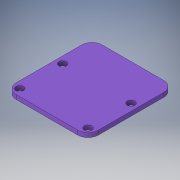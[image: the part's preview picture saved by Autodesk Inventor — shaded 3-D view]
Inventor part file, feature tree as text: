
AUTODESK INVENTOR PART (.ipt)
format: ipt  version: 2019.2 (Build 232265000, 265)  size: 130,048 bytes
history: native  units: in
note: dims shown in document units (in); Inventor stores cm internally (conversion verified against a paired STEP export)
features: sketch x2, extrude x1, fillet x1, hole x1
ambient origin geometry x8: Origin, YZ Plane, XZ Plane, XY Plane, X Axis, Y Axis, Z Axis, Center Point
bodies: Solid1 (feature_tree)
feature tree (5):
  extrude  "Extrusion1"  Depth=0.9843in
  fillet  "Fillet1"  Radius=0.05in
  hole  "Hole2"  [1 undecoded]
  sketch  "Sketch1"  dims[d0=0.9394in d1=0.9843in d4=0.05in d5=0.0in]
  sketch  "Sketch3"  dims[d15=0.1181in d16=0.0787in d17=0.0787in d18=0.0787in d19=0.5709in d20=0.0866in d21=0.75in d22=0.375in d23=0.25in d24=0.5635in d25=1.0in d26=0.8108in]
note: 1 required parameter value undecoded (feature->parameter linkage not recoverable at this tier; creation-order binding heuristic only, values carry confidence <= 0.55)
